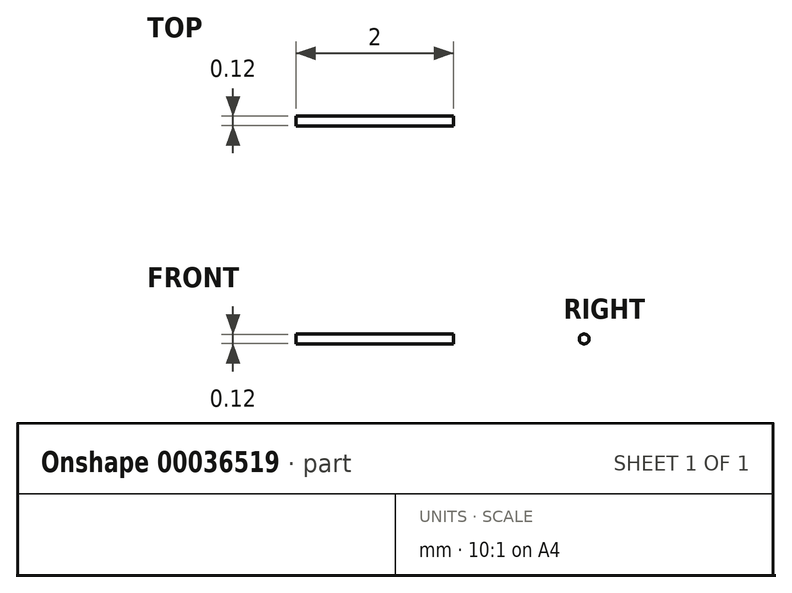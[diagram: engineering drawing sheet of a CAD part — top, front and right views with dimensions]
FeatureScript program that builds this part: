
annotation { "Feature Type Name" : "Feature", "Feature Type Description" : "" }
export const myFeature = defineFeature(function(context is Context, id is Id, definition is map)
    precondition{}
    {
        {
            var Q0;
            Q0=qCreatedBy(makeId("Right.planeOp"),FACE);
            var sketch = newSketch(context, id + "F0", { "sketchPlane" : qUnion([Q0])});
            skCircle(sketch, "E0", {"center": v(0, 0) * mm, "radius": 0.06 * mm});
            skSolve(sketch);
        }
        {
            var Q0;
            Q0=qSketchRegion(id+"F0",true);
            extrude(context, id + "F1", {"entities" : qUnion([Q0]), "depth" : 2 * mm, "offsetDistance" : 25 * mm});
        }
    });
